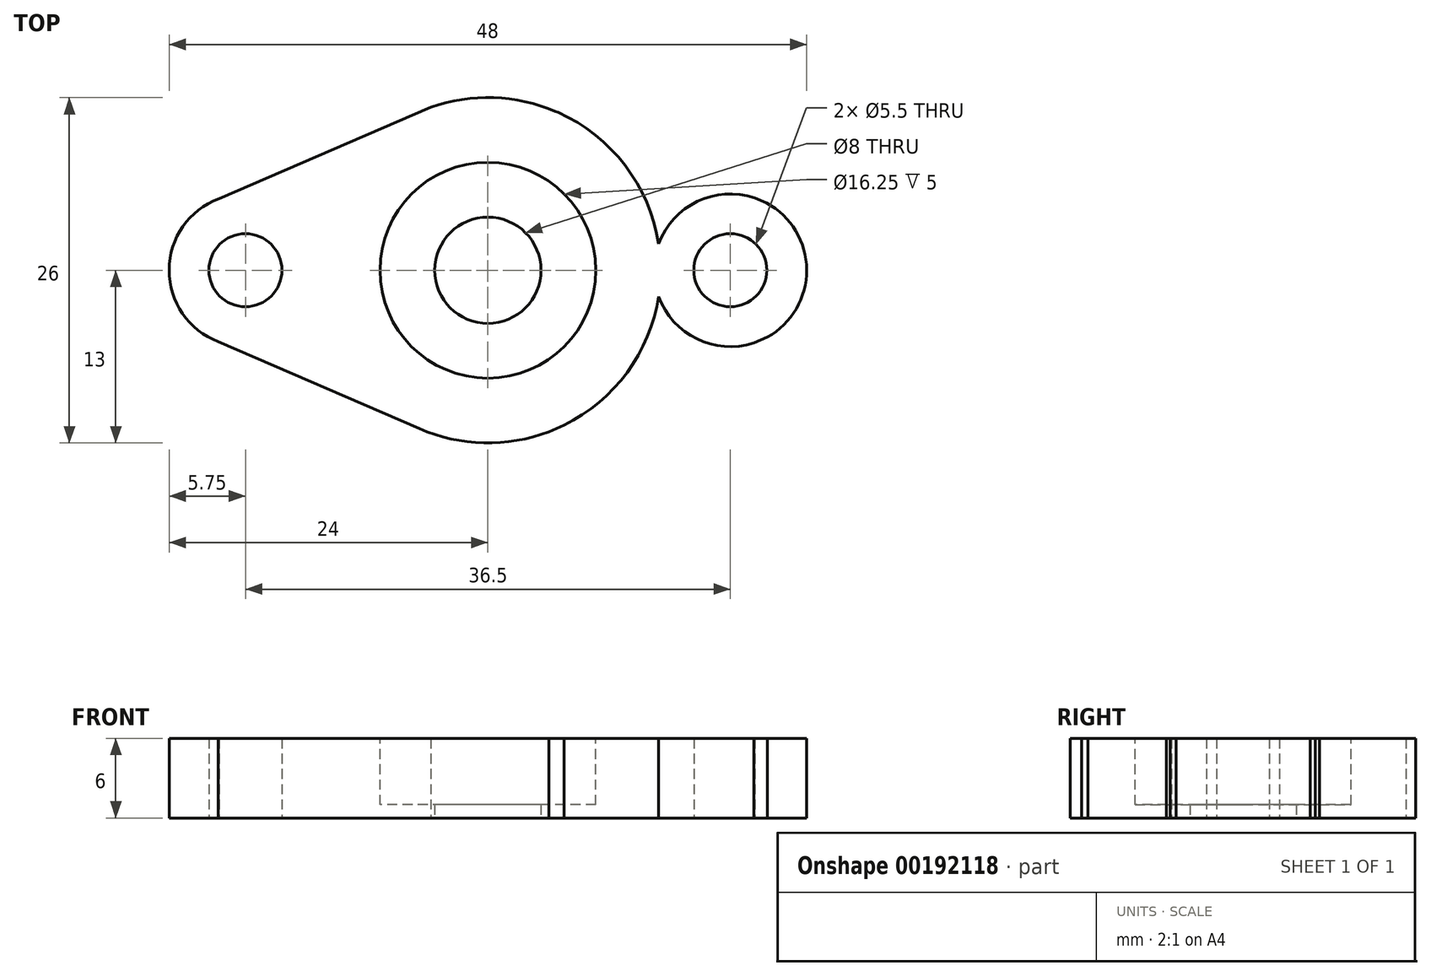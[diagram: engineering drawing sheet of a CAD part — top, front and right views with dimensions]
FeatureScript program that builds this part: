
annotation { "Feature Type Name" : "Feature", "Feature Type Description" : "" }
export const myFeature = defineFeature(function(context is Context, id is Id, definition is map)
    precondition{}
    {
        {
            var Q0;
            Q0=qCreatedBy(makeId("Top.planeOp"),FACE);
            var sketch = newSketch(context, id + "F0", { "sketchPlane" : qUnion([Q0])});
            skCircle(sketch, "E0", {"center": v(0, 0) * mm, "radius": 13 * mm});
            skCircle(sketch, "E1", {"center": v(18.25, 0) * mm, "radius": 2.75 * mm});
            skCircle(sketch, "E2", {"center": v(18.25, 0) * mm, "radius": 5.75 * mm});
            skLineSegment(sketch, "E3", {"start": v(5.08, 11.97) * mm, "end": v(20.98, 5.06) * mm});
            skLineSegment(sketch, "E4", {"start": v(4.59, -12.16) * mm, "end": v(21.04, -5.03) * mm});
            skCircle(sketch, "E5", {"center": v(-18.25, 0) * mm, "radius": 2.75 * mm});
            skCircle(sketch, "E6", {"center": v(-18.25, 0) * mm, "radius": 5.75 * mm});
            skCircle(sketch, "E7", {"center": v(0, 0) * mm, "radius": 4 * mm});
            skLineSegment(sketch, "E8", {"start": v(-20.25, 5.39) * mm, "end": v(-4.28, 12.27) * mm});
            skLineSegment(sketch, "E9", {"start": v(-20.3, -5.38) * mm, "end": v(-5.17, -11.93) * mm});
            skSolve(sketch);
        }
        {
            var Q0;
            Q0=makeQuery(id+"F0.imprint","IMPRINT",FACE,{"disambiguationData":[TD([[makeQuery(id+"F0.imprint","IMPRINT",EDGE,{"derivedFrom":sQuery(id+"F0.wireOp",EDGE,"E1")}),-1.0]])]});
            var Q1;
            {var subQ0=sQuery(id+"F0.wireOp",EDGE,"E3");var subQ1=sQuery(id+"F0.wireOp",EDGE,"E0");var subQ2=makeQuery(id+"F0.imprint","INTERSECT",VERTEX,{"disambiguationData":[OD(1.0)],"derivedFrom":[subQ1,subQ0]});Q1=makeQuery(id+"F0.imprint","IMPRINT",FACE,{"disambiguationData":[TD([[makeQuery(id+"F0.imprint","IMPRINT",EDGE,{"disambiguationData":[TD([[subQ2,1.0]])],"derivedFrom":subQ1}),-1.0]])]});}
            var Q2;
            {var subQ0=sQuery(id+"F0.wireOp",EDGE,"E2");var subQ1=sQuery(id+"F0.wireOp",EDGE,"E0");var subQ2=makeQuery(id+"F0.imprint","INTERSECT",VERTEX,{"disambiguationData":[OD(0.0)],"derivedFrom":[subQ1,subQ0]});Q2=makeQuery(id+"F0.imprint","IMPRINT",FACE,{"disambiguationData":[TD([[makeQuery(id+"F0.imprint","IMPRINT",EDGE,{"disambiguationData":[TD([[subQ2,1.0]])],"derivedFrom":subQ1}),1.0]])]});}
            var Q3;
            {var subQ0=sQuery(id+"F0.wireOp",EDGE,"E4");var subQ1=sQuery(id+"F0.wireOp",EDGE,"E0");var subQ2=makeQuery(id+"F0.imprint","INTERSECT",VERTEX,{"disambiguationData":[OD(1.0)],"derivedFrom":[subQ1,subQ0]});Q3=makeQuery(id+"F0.imprint","IMPRINT",FACE,{"disambiguationData":[TD([[makeQuery(id+"F0.imprint","IMPRINT",EDGE,{"disambiguationData":[TD([[subQ2,-1.0]])],"derivedFrom":subQ1}),-1.0]])]});}
            var Q4;
            Q4=makeQuery(id+"F0.imprint","IMPRINT",FACE,{"disambiguationData":[TD([[makeQuery(id+"F0.imprint","IMPRINT",EDGE,{"derivedFrom":sQuery(id+"F0.wireOp",EDGE,"E7")}),-1.0]])]});
            var Q5;
            {var subQ0=sQuery(id+"F0.wireOp",EDGE,"bA9I7gj6-ncfJ-UPCZ-OF19-VHGP0GgZUe2g");var subQ1=sQuery(id+"F0.wireOp",EDGE,"E0");var subQ2=makeQuery(id+"F0.imprint","INTERSECT",VERTEX,{"disambiguationData":[OD(1.0)],"derivedFrom":[subQ1,subQ0]});Q5=makeQuery(id+"F0.imprint","IMPRINT",FACE,{"disambiguationData":[TD([[makeQuery(id+"F0.imprint","IMPRINT",EDGE,{"disambiguationData":[TD([[subQ2,-1.0]])],"derivedFrom":subQ1}),-1.0]])]});}
            var Q6;
            Q6=makeQuery(id+"F0.imprint","IMPRINT",FACE,{"disambiguationData":[TD([[makeQuery(id+"F0.imprint","IMPRINT",EDGE,{"derivedFrom":sQuery(id+"F0.wireOp",EDGE,"E5")}),-1.0]])]});
            var Q7;
            {var subQ0=sQuery(id+"F0.wireOp",EDGE,"e7J1H7He-lFNz-ih7A-tEbb-5a1sqnkIgTCI");Q7=makeQuery(id+"F0.imprint","IMPRINT",FACE,{"disambiguationData":[TD([[makeQuery(id+"F0.imprint","IMPRINT",EDGE,{"derivedFrom":subQ0}),1.0]])]});}
            var Q8;
            {var subQ0=sQuery(id+"F0.wireOp",EDGE,"E6");var subQ1=sQuery(id+"F0.wireOp",EDGE,"E0");var subQ2=makeQuery(id+"F0.imprint","INTERSECT",VERTEX,{"disambiguationData":[OD(0.0)],"derivedFrom":[subQ1,subQ0]});Q8=makeQuery(id+"F0.imprint","IMPRINT",FACE,{"disambiguationData":[TD([[makeQuery(id+"F0.imprint","IMPRINT",EDGE,{"disambiguationData":[TD([[subQ2,-1.0]])],"derivedFrom":subQ1}),1.0]])]});}
            var Q9;
            {var subQ0=sQuery(id+"F0.wireOp",EDGE,"E8");var subQ1=sQuery(id+"F0.wireOp",EDGE,"E0");var subQ2=makeQuery(id+"F0.imprint","INTERSECT",VERTEX,{"disambiguationData":[OD(1.0)],"derivedFrom":[subQ1,subQ0]});Q9=makeQuery(id+"F0.imprint","IMPRINT",FACE,{"disambiguationData":[TD([[makeQuery(id+"F0.imprint","IMPRINT",EDGE,{"disambiguationData":[TD([[subQ2,-1.0]])],"derivedFrom":subQ1}),-1.0]])]});}
            var Q10;
            {var subQ0=sQuery(id+"F0.wireOp",EDGE,"E9");Q10=makeQuery(id+"F0.imprint","IMPRINT",FACE,{"disambiguationData":[TD([[makeQuery(id+"F0.imprint","IMPRINT",EDGE,{"derivedFrom":subQ0}),1.0]])]});}
            extrude(context, id + "F1", {"entities" : qUnion([Q0, Q1, Q2, Q3, Q4, Q5, Q6, Q7, Q8, Q9, Q10]), "depth" : 6 * mm});
        }
        {
            var Q0;
            Q0=makeQuery(id+"F1.opExtrude","CAP_FACE",FACE,{"disambiguationData":[OSD([sQuery(id+"F0.wireOp",EDGE,"E0"),sQuery(id+"F0.wireOp",EDGE,"E1"),sQuery(id+"F0.wireOp",EDGE,"E2"),sQuery(id+"F0.wireOp",EDGE,"E3"),sQuery(id+"F0.wireOp",EDGE,"E4"),sQuery(id+"F0.wireOp",EDGE,"E5"),sQuery(id+"F0.wireOp",EDGE,"E6"),sQuery(id+"F0.wireOp",EDGE,"E7"),sQuery(id+"F0.wireOp",EDGE,"E8"),sQuery(id+"F0.wireOp",EDGE,"E9")])],"isStart":false});
            var sketch = newSketch(context, id + "F2", { "sketchPlane" : qUnion([Q0])});
            skCircle(sketch, "E10", {"center": v(0, 0) * mm, "radius": 8.12 * mm});
            skSolve(sketch);
        }
        {
            var Q0;
            Q0=makeQuery(id+"F2.imprint","IMPRINT",FACE,{"disambiguationData":[TD([[makeQuery(id+"F2.imprint","IMPRINT",EDGE,{"derivedFrom":sQuery(id+"F2.wireOp",EDGE,"E10")}),1.0]])]});
            extrude(context, id + "F3", {"entities" : qUnion([Q0]), "operationType" : NewBodyOperationType.REMOVE, "oppositeDirection" : true, "depth" : 5 * mm});
        }
    });
